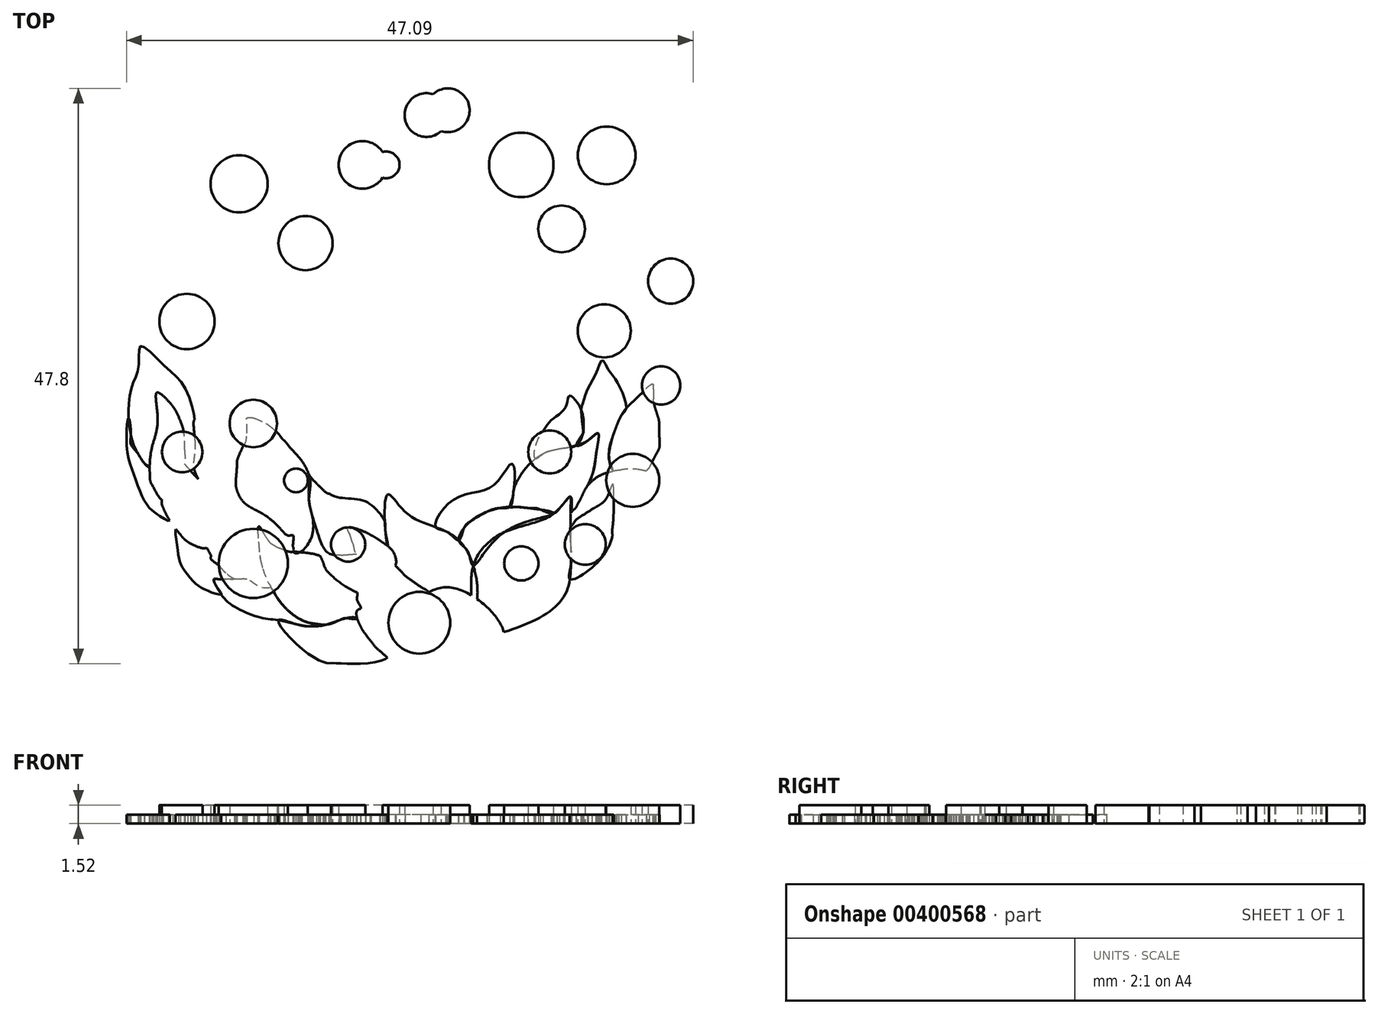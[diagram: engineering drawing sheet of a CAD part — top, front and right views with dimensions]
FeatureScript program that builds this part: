
annotation { "Feature Type Name" : "Feature", "Feature Type Description" : "" }
export const myFeature = defineFeature(function(context is Context, id is Id, definition is map)
    precondition{}
    {
        {
            var Q0;
            Q0=qCreatedBy(makeId("Top.planeOp"),FACE);
            var sketch = newSketch(context, id + "F0", { "sketchPlane" : qUnion([Q0])});
            skCircle(sketch, "E0", {"center": v(13.2, 35.87) * mm, "radius": 2.4 * mm});
            skCircle(sketch, "E1", {"center": v(-7.1, 35.08) * mm, "radius": 1.98 * mm});
            skCircle(sketch, "E2", {"center": v(-5.11, 35.08) * mm, "radius": 1.1 * mm});
            skCircle(sketch, "E3", {"center": v(-21.68, 22.07) * mm, "radius": 2.3 * mm});
            skCircle(sketch, "E4", {"center": v(-16.16, 13.6) * mm, "radius": 1.97 * mm});
            skCircle(sketch, "E5", {"center": v(-16.16, 1.97) * mm, "radius": 2.87 * mm});
            skCircle(sketch, "E6", {"center": v(-2.36, -2.96) * mm, "radius": 2.57 * mm});
            skCircle(sketch, "E7", {"center": v(6.1, 1.97) * mm, "radius": 1.42 * mm});
            skCircle(sketch, "E8", {"center": v(15.37, 8.87) * mm, "radius": 2.2 * mm});
            skCircle(sketch, "E9", {"center": v(13, 21.28) * mm, "radius": 2.2 * mm});
            skCircle(sketch, "E10", {"center": v(9.46, 29.76) * mm, "radius": 1.94 * mm});
            skCircle(sketch, "E11", {"center": v(-11.82, 28.58) * mm, "radius": 2.25 * mm});
            skCircle(sketch, "E12", {"center": v(6.1, 35.08) * mm, "radius": 2.68 * mm});
            skCircle(sketch, "E13", {"center": v(18.52, 25.42) * mm, "radius": 1.87 * mm});
            skSolve(sketch);
        }
        {
            var Q0;
            Q0=qCreatedBy(makeId("Top.planeOp"),FACE);
            var sketch = newSketch(context, id + "F1", { "sketchPlane" : qUnion([Q0])});
            skCircle(sketch, "E14", {"center": v(0, 39.61) * mm, "radius": 1.82 * mm});
            skCircle(sketch, "E15", {"center": v(-1.77, 39.22) * mm, "radius": 1.82 * mm});
            skCircle(sketch, "E16", {"center": v(-17.34, 33.5) * mm, "radius": 2.37 * mm});
            skCircle(sketch, "E17", {"center": v(-22.07, 11.23) * mm, "radius": 1.68 * mm});
            skCircle(sketch, "E18", {"center": v(-12.61, 8.87) * mm, "radius": 0.99 * mm});
            skCircle(sketch, "E19", {"center": v(-8.28, 3.55) * mm, "radius": 1.42 * mm});
            skCircle(sketch, "E20", {"center": v(8.47, 11.23) * mm, "radius": 1.78 * mm});
            skCircle(sketch, "E21", {"center": v(11.43, 3.55) * mm, "radius": 1.7 * mm});
            skCircle(sketch, "E22", {"center": v(17.74, 16.75) * mm, "radius": 1.59 * mm});
            skSolve(sketch);
        }
        {
            var Q0;
            Q0=qCreatedBy(makeId("Top.planeOp"),FACE);
            var sketch = newSketch(context, id + "F2", { "sketchPlane" : qUnion([Q0])});
            skFitSpline(sketch, "E23", {"points": [v(1.92, -3.92) * mm, v(1.92, -1.95) * mm, v(2.12, 1.8) * mm, v(4.68, 4.55) * mm, v(8.82, 6.13) * mm, v(10.2, 7.51) * mm, v(10.2, 4.55) * mm, v(10, 0) * mm, v(7.24, -2.74) * mm, v(1.92, -3.92) * mm]});
            skFitSpline(sketch, "E24", {"points": [v(2.12, 1.8) * mm, v(0, 4.55) * mm, v(-3.4, 6.13) * mm, v(-4.98, 7.7) * mm, v(-5.17, 4.55) * mm, v(-4.38, 1.8) * mm, v(-2.22, 0) * mm, v(1.92, -1.95) * mm, v(2.12, 1.8) * mm]});
            skFitSpline(sketch, "E25", {"points": [v(4.68, -3.92) * mm, v(1.92, -6.28) * mm, v(-4.38, -6.28) * mm, v(-7.54, -1.95) * mm, v(-4.38, -1.95) * mm, v(0, 0) * mm, v(4.68, -3.92) * mm]});
            skFitSpline(sketch, "E26", {"points": [v(0.92, 3.9) * mm, v(1.92, 5.5) * mm, v(4.35, 6.58) * mm, v(6.67, 6.58) * mm, v(8.82, 6.13) * mm, v(4.68, 4.55) * mm, v(2.12, 1.8) * mm, v(1.78, 2.66) * mm, v(1.42, 3.3) * mm, v(0.92, 3.9) * mm]});
            skFitSpline(sketch, "E27", {"points": [v(10.15, 0.66) * mm, v(12.18, 1.8) * mm, v(13.59, 3.9) * mm, v(13.75, 5.54) * mm, v(13.71, 8.57) * mm, v(13.22, 7.45) * mm, v(12.3, 6.66) * mm, v(10.69, 5.62) * mm, v(10.22, 5.06) * mm, v(10.2, 3.62) * mm, v(10.23, 1.8) * mm, v(10.15, 0.66) * mm]});
            skFitSpline(sketch, "E28", {"points": [v(-5.02, -5.85) * mm, v(-7.13, -6.35) * mm, v(-9.49, -6.3) * mm, v(-10.2, -6.27) * mm, v(-12.43, -4.86) * mm, v(-14.09, -2.74) * mm, v(-12.43, -3.12) * mm, v(-10.32, -3.16) * mm, v(-9, -2.74) * mm, v(-7.54, -2.57) * mm, v(-7.23, -3.27) * mm, v(-6.83, -3.92) * mm, v(-6.47, -4.4) * mm, v(-5.59, -5.35) * mm, v(-5.02, -5.85) * mm]});
            skFitSpline(sketch, "E29", {"points": [v(-3.53, 0.94) * mm, v(-4.38, 1.8) * mm, v(-6.3, 2.64) * mm, v(-8.29, 2.68) * mm, v(-9.9, 2.8) * mm, v(-10.65, 3.14) * mm, v(-10.23, 1.8) * mm, v(-9.32, 0.66) * mm, v(-7.54, -0.42) * mm, v(-5.02, -0.92) * mm, v(-3.4, -0.92) * mm, v(-2.11, -0.76) * mm, v(-1.6, -0.44) * mm, v(-2.22, 0) * mm, v(-3.16, 0.66) * mm, v(-3.53, 0.94) * mm]});
            skFitSpline(sketch, "E30", {"points": [v(-10.14, -3.12) * mm, v(-12.43, -2.57) * mm, v(-14.25, -0.76) * mm, v(-15.58, 2.35) * mm, v(-15.7, 5.04) * mm, v(-14.91, 3.9) * mm, v(-12.84, 2.97) * mm, v(-10.56, 2.54) * mm, v(-10.32, 1.96) * mm, v(-9.76, 1.09) * mm, v(-7.54, -0.42) * mm, v(-7.54, -1) * mm, v(-7.23, -1.8) * mm, v(-7.54, -1.95) * mm, v(-7.54, -2.57) * mm, v(-8.42, -2.57) * mm, v(-9, -2.74) * mm, v(-10.14, -3.12) * mm]});
            skFitSpline(sketch, "E31", {"points": [v(-5.02, 3.44) * mm, v(-5.68, 3.9) * mm, v(-6.83, 4.55) * mm, v(-8.29, 4.92) * mm, v(-7.95, 3.9) * mm, v(-7.54, 2.68) * mm, v(-6.3, 2.64) * mm, v(-5.66, 2.47) * mm, v(-5.02, 2.2) * mm, v(-4.38, 1.8) * mm, v(-4.38, 2.64) * mm, v(-5.02, 3.44) * mm]});
            skFitSpline(sketch, "E32", {"points": [v(-14.72, 0) * mm, v(-16.7, 0.66) * mm, v(-19.02, 0.66) * mm, v(-19.43, 0.66) * mm, v(-19.18, 0) * mm, v(-18.44, -1.09) * mm, v(-17.11, -1.95) * mm, v(-15.37, -2.57) * mm, v(-14.09, -2.74) * mm, v(-12.43, -3.12) * mm, v(-11.56, -3.25) * mm, v(-10.32, -3.16) * mm, v(-11.55, -2.95) * mm, v(-12.43, -2.57) * mm, v(-13.26, -1.95) * mm, v(-14.25, -0.76) * mm, v(-14.72, 0) * mm]});
            skFitSpline(sketch, "E33", {"points": [v(-1, 4.98) * mm, v(-0.64, 6.13) * mm, v(0.92, 7.51) * mm, v(3, 8.06) * mm, v(4.35, 9.05) * mm, v(5.33, 10.25) * mm, v(5.57, 9.3) * mm, v(5.4, 7.51) * mm, v(5.17, 6.66) * mm, v(4.35, 6.58) * mm, v(3.3, 6.28) * mm, v(1.92, 5.5) * mm, v(1.34, 4.91) * mm, v(0.92, 3.9) * mm, v(0, 4.55) * mm, v(-1, 4.98) * mm]});
            skFitSpline(sketch, "E34", {"points": [v(5.48, 8.06) * mm, v(6.28, 9.63) * mm, v(7.94, 11.08) * mm, v(9.63, 11.54) * mm, v(11.66, 12.2) * mm, v(12.5, 12.78) * mm, v(12.4, 11.58) * mm, v(12, 9.3) * mm, v(11.13, 7.51) * mm, v(10.23, 6.13) * mm, v(10.2, 7.51) * mm, v(9.7, 7.04) * mm, v(9.3, 6.58) * mm, v(8.82, 6.13) * mm, v(7.7, 6.44) * mm, v(7.24, 6.58) * mm, v(6.67, 6.58) * mm, v(5.57, 6.66) * mm, v(5.17, 6.66) * mm, v(5.4, 7.51) * mm, v(5.48, 8.06) * mm]});
            skFitSpline(sketch, "E35", {"points": [v(11.64, 8.46) * mm, v(12.78, 9.34) * mm, v(14.23, 9.71) * mm, v(15.8, 9.8) * mm, v(17.1, 9.67) * mm, v(18.33, 9.96) * mm, v(18.38, 9.5) * mm, v(18.13, 8.3) * mm, v(17.3, 6.65) * mm, v(16.01, 5.4) * mm, v(14.07, 4.5) * mm, v(13.7, 4.36) * mm, v(13.75, 5.54) * mm, v(13.78, 6.6) * mm, v(13.8, 7.85) * mm, v(13.71, 8.57) * mm, v(13.44, 7.98) * mm, v(13.22, 7.45) * mm, v(12.64, 6.85) * mm, v(12.3, 6.66) * mm, v(11.13, 5.93) * mm, v(10.69, 5.62) * mm, v(10.22, 5.06) * mm, v(10.22, 5.62) * mm, v(10.23, 6.13) * mm, v(10.69, 6.66) * mm, v(11.13, 7.51) * mm, v(11.64, 8.46) * mm]});
            skFitSpline(sketch, "E36", {"points": [v(-5.24, 5.45) * mm, v(-6.1, 6.6) * mm, v(-7.14, 7.23) * mm, v(-8.6, 7.4) * mm, v(-9.88, 7.77) * mm, v(-11.37, 9.13) * mm, v(-11.5, 9.3) * mm, v(-11.5, 9.01) * mm, v(-11.54, 8.55) * mm, v(-11.54, 7.27) * mm, v(-11.29, 6.03) * mm, v(-10.75, 4.29) * mm, v(-9.9, 2.8) * mm, v(-8.88, 2.65) * mm, v(-8.29, 2.68) * mm, v(-7.54, 2.68) * mm, v(-7.88, 3.6) * mm, v(-8.12, 4.3) * mm, v(-8.29, 4.92) * mm, v(-6.83, 4.55) * mm, v(-6.3, 4.28) * mm, v(-5.68, 3.9) * mm, v(-5.02, 3.44) * mm, v(-5.17, 4.55) * mm, v(-5.24, 5.45) * mm]});
            skFitSpline(sketch, "E37", {"points": [v(-17.7, 0.68) * mm, v(-19.02, 1.8) * mm, v(-19.68, 2.66) * mm, v(-20.43, 4.3) * mm, v(-20.6, 6.13) * mm, v(-20.5, 8.06) * mm, v(-20.01, 8.06) * mm, v(-17.53, 6.83) * mm, v(-14.72, 5.62) * mm, v(-12.84, 2.97) * mm, v(-14.4, 3.44) * mm, v(-14.91, 3.9) * mm, v(-15.7, 5.04) * mm, v(-15.7, 3.44) * mm, v(-15.58, 2.35) * mm, v(-14.91, 0.37) * mm, v(-14.72, 0) * mm, v(-15.58, 0) * mm, v(-16.7, 0.66) * mm, v(-17.7, 0.68) * mm]});
            skFitSpline(sketch, "E38", {"points": [v(-16.7, 6.83) * mm, v(-17.53, 8.06) * mm, v(-17.53, 10.48) * mm, v(-16.7, 12.8) * mm, v(-16.7, 14.04) * mm, v(-14.91, 13.46) * mm, v(-13.26, 11.8) * mm, v(-11.5, 9.3) * mm, v(-11.54, 7.27) * mm, v(-11.29, 6.03) * mm, v(-11.29, 4.29) * mm, v(-12.27, 2.9) * mm, v(-12.84, 2.97) * mm, v(-12.84, 4.3) * mm, v(-13.26, 4.29) * mm, v(-14.72, 5.62) * mm, v(-16.7, 6.83) * mm]});
            skFitSpline(sketch, "E39", {"points": [v(7.28, 10.66) * mm, v(7.33, 11.86) * mm, v(7.94, 13) * mm, v(8.66, 13.93) * mm, v(9.8, 14.96) * mm, v(10.1, 15.9) * mm, v(10.69, 15.45) * mm, v(11.22, 14.27) * mm, v(11.22, 12.74) * mm, v(10.69, 11.77) * mm, v(9.63, 11.54) * mm, v(8.58, 11.32) * mm, v(7.94, 11.08) * mm, v(7.28, 10.66) * mm]});
            skFitSpline(sketch, "E40", {"points": [v(16.53, 9.67) * mm, v(17.1, 10.63) * mm, v(17.58, 11.58) * mm, v(17.58, 12.65) * mm, v(17.53, 13.93) * mm, v(17.1, 15.6) * mm, v(17.1, 16.83) * mm, v(16.7, 16.69) * mm, v(16.2, 16.2) * mm, v(15.26, 15.3) * mm, v(14.43, 14.27) * mm, v(13.69, 12.45) * mm, v(13.4, 11.08) * mm, v(13.73, 9.63) * mm, v(14.23, 9.71) * mm, v(15.8, 9.8) * mm, v(16.53, 9.67) * mm]});
            skFitSpline(sketch, "E41", {"points": [v(14.83, 14.85) * mm, v(14.43, 16.34) * mm, v(13.83, 17.42) * mm, v(13.34, 18.07) * mm, v(12.85, 18.85) * mm, v(12.4, 17.97) * mm, v(11.66, 16.54) * mm, v(11.22, 15.3) * mm, v(11.1, 14.7) * mm, v(11.27, 13) * mm, v(11.22, 12.74) * mm, v(10.69, 11.77) * mm, v(11.66, 12.2) * mm, v(12.5, 12.78) * mm, v(12.4, 11.58) * mm, v(12.3, 10.82) * mm, v(12, 9.3) * mm, v(11.64, 8.46) * mm, v(12.78, 9.34) * mm, v(13.73, 9.63) * mm, v(13.44, 10.48) * mm, v(13.4, 11.08) * mm, v(13.69, 12.45) * mm, v(14.08, 13.52) * mm, v(14.43, 14.27) * mm, v(14.83, 14.85) * mm]});
            skFitSpline(sketch, "E42", {"points": [v(-20.03, 3.3) * mm, v(-21.35, 3.6) * mm, v(-22.17, 4.3) * mm, v(-23.1, 5.54) * mm, v(-23.75, 7) * mm, v(-23.63, 8.06) * mm, v(-23.34, 9.63) * mm, v(-23.16, 11.32) * mm, v(-21.35, 9.63) * mm, v(-20.01, 8.06) * mm, v(-20.5, 8.06) * mm, v(-20.63, 7.3) * mm, v(-20.6, 6.13) * mm, v(-20.5, 4.7) * mm, v(-20.43, 4.3) * mm, v(-20.03, 3.3) * mm]});
            skFitSpline(sketch, "E43", {"points": [v(-9.88, 7.77) * mm, v(-10.5, 9.3) * mm, v(-11.39, 10.48) * mm, v(-13.26, 11.8) * mm, v(-12.13, 10.48) * mm, v(-11.5, 9.3) * mm, v(-10.75, 8.46) * mm, v(-9.88, 7.77) * mm]});
            skFitSpline(sketch, "E44", {"points": [v(18.26, 8.84) * mm, v(18.83, 9.5) * mm, v(19.6, 11.08) * mm, v(20, 13.46) * mm, v(19.68, 15.3) * mm, v(19.2, 16.83) * mm, v(18.7, 17.99) * mm, v(18.38, 19.62) * mm, v(18.13, 19.1) * mm, v(17.8, 18.46) * mm, v(17.58, 17.9) * mm, v(17.3, 17.18) * mm, v(17.1, 16.83) * mm, v(17.1, 16.06) * mm, v(17.1, 15.6) * mm, v(17.3, 14.68) * mm, v(17.53, 13.93) * mm, v(17.58, 13.46) * mm, v(17.58, 12.65) * mm, v(17.61, 12.04) * mm, v(17.58, 11.58) * mm, v(17.2, 10.8) * mm, v(17.1, 10.48) * mm, v(16.73, 9.9) * mm, v(16.53, 9.67) * mm, v(17.1, 9.67) * mm, v(17.58, 9.67) * mm, v(18.33, 9.96) * mm, v(18.38, 9.5) * mm, v(18.26, 8.84) * mm]});
            skFitSpline(sketch, "E45", {"points": [v(-18.84, -0.6) * mm, v(-20.01, -0.28) * mm, v(-21.05, 0.39) * mm, v(-22.13, 1.8) * mm, v(-22.44, 3.03) * mm, v(-22.6, 4.83) * mm, v(-22.17, 4.3) * mm, v(-21.61, 3.77) * mm, v(-21.35, 3.6) * mm, v(-20.63, 3.44) * mm, v(-20.03, 3.3) * mm, v(-19.68, 2.66) * mm, v(-19.68, 2.35) * mm, v(-19.02, 1.8) * mm, v(-18.44, 1.17) * mm, v(-17.7, 0.68) * mm, v(-18.44, 0.66) * mm, v(-19.02, 0.66) * mm, v(-19.43, 0.66) * mm, v(-19.18, 0) * mm, v(-18.84, -0.6) * mm]});
            skFitSpline(sketch, "E46", {"points": [v(-13.6, 12.2) * mm, v(-13.72, 13.93) * mm, v(-14.4, 15.6) * mm, v(-15.58, 17.62) * mm, v(-16.7, 18.46) * mm, v(-17.7, 19.3) * mm, v(-19.02, 20.58) * mm, v(-19.02, 19.89) * mm, v(-19.18, 18.8) * mm, v(-19.18, 17.59) * mm, v(-19.18, 15.92) * mm, v(-19.02, 14.77) * mm, v(-18.44, 13.46) * mm, v(-16.95, 11.86) * mm, v(-16.7, 12.8) * mm, v(-16.7, 13.52) * mm, v(-16.7, 14.04) * mm, v(-16.13, 14.04) * mm, v(-14.91, 13.46) * mm, v(-14.32, 13) * mm, v(-13.98, 12.65) * mm, v(-13.6, 12.2) * mm]});
            skFitSpline(sketch, "E47", {"points": [v(-20.43, 8.46) * mm, v(-21.04, 9.96) * mm, v(-21.04, 11.08) * mm, v(-21, 12.2) * mm, v(-21.04, 13.93) * mm, v(-20.01, 13) * mm, v(-19.02, 12.45) * mm, v(-17.7, 11.08) * mm, v(-17.53, 10.48) * mm, v(-17.53, 9.96) * mm, v(-17.62, 8.46) * mm, v(-17.53, 8.06) * mm, v(-16.9, 7) * mm, v(-15.86, 6.28) * mm, v(-16.85, 6.6) * mm, v(-17.53, 6.83) * mm, v(-18.94, 7.51) * mm, v(-19.42, 7.77) * mm, v(-20.01, 8.06) * mm, v(-20.43, 8.46) * mm]});
            skFitSpline(sketch, "E48", {"points": [v(-23.75, 7.3) * mm, v(-24.45, 8.3) * mm, v(-24.76, 9.5) * mm, v(-24.6, 11.58) * mm, v(-24.1, 13.93) * mm, v(-24.17, 16.16) * mm, v(-23.1, 15.3) * mm, v(-22.17, 13.46) * mm, v(-21.9, 10.26) * mm, v(-22.23, 10.63) * mm, v(-23.02, 11.32) * mm, v(-23.16, 11.32) * mm, v(-23.16, 11.08) * mm, v(-23.16, 10.48) * mm, v(-23.34, 9.63) * mm, v(-23.52, 8.46) * mm, v(-23.63, 8.06) * mm, v(-23.75, 7.3) * mm]});
            skFitSpline(sketch, "E49", {"points": [v(-24.78, 9.96) * mm, v(-25.74, 11.08) * mm, v(-26.33, 12.65) * mm, v(-26.54, 14.73) * mm, v(-26.2, 16.83) * mm, v(-25.67, 18.46) * mm, v(-25.53, 20.03) * mm, v(-23.63, 18.46) * mm, v(-21.8, 16.5) * mm, v(-21.04, 13.93) * mm, v(-21.04, 13.52) * mm, v(-21, 12.2) * mm, v(-21, 11.86) * mm, v(-21.04, 11.08) * mm, v(-21.04, 9.67) * mm, v(-20.43, 8.46) * mm, v(-21.35, 9.63) * mm, v(-21.9, 10.26) * mm, v(-21.9, 11.08) * mm, v(-21.9, 12.65) * mm, v(-22.33, 14.04) * mm, v(-22.86, 15.03) * mm, v(-23.22, 15.45) * mm, v(-24.17, 16.16) * mm, v(-24.17, 15.3) * mm, v(-24.1, 14.04) * mm, v(-24.1, 13.46) * mm, v(-24.1, 12.65) * mm, v(-24.6, 11.58) * mm, v(-24.78, 9.96) * mm]});
            skFitSpline(sketch, "E50", {"points": [v(-23.1, 5.54) * mm, v(-24.1, 6.03) * mm, v(-25.11, 7) * mm, v(-26.02, 9.13) * mm, v(-26.68, 11.77) * mm, v(-26.52, 14.04) * mm, v(-26.33, 12.65) * mm, v(-26.33, 11.86) * mm, v(-25.74, 11.08) * mm, v(-25.19, 10.26) * mm, v(-24.78, 9.96) * mm, v(-24.76, 9.13) * mm, v(-24.45, 8.3) * mm, v(-23.75, 7.3) * mm, v(-23.75, 6.83) * mm, v(-23.1, 5.54) * mm]});
            skSolve(sketch);
        }
        {
            var Q0;
            Q0 = qSketchRegion(id + "F0", true);
            var Q1;
            Q1=makeQuery(id+"F1.imprint","IMPRINT",FACE,{"disambiguationData":[TD([[makeQuery(id+"F1.imprint","IMPRINT",EDGE,{"derivedFrom":sQuery(id+"F1.wireOp",EDGE,"E16")}),1.0]])]});
            var Q2;
            {var subQ0=sQuery(id+"F1.wireOp",EDGE,"E15");var subQ1=sQuery(id+"F1.wireOp",EDGE,"E14");var subQ2=makeQuery(id+"F1.imprint","INTERSECT",VERTEX,{"disambiguationData":[OD(0.0)],"derivedFrom":[subQ1,subQ0]});Q2=makeQuery(id+"F1.imprint","IMPRINT",FACE,{"disambiguationData":[TD([[makeQuery(id+"F1.imprint","IMPRINT",EDGE,{"disambiguationData":[TD([[subQ2,1.0]])],"derivedFrom":subQ1}),-1.0]])]});}
            var Q3;
            {var subQ0=sQuery(id+"F1.wireOp",EDGE,"E15");var subQ1=sQuery(id+"F1.wireOp",EDGE,"E14");var subQ2=makeQuery(id+"F1.imprint","INTERSECT",VERTEX,{"disambiguationData":[OD(0.0)],"derivedFrom":[subQ1,subQ0]});Q3=makeQuery(id+"F1.imprint","IMPRINT",FACE,{"disambiguationData":[TD([[makeQuery(id+"F1.imprint","IMPRINT",EDGE,{"disambiguationData":[TD([[subQ2,1.0]])],"derivedFrom":subQ1}),1.0]])]});}
            var Q4;
            {var subQ0=sQuery(id+"F1.wireOp",EDGE,"E15");var subQ1=sQuery(id+"F1.wireOp",EDGE,"E14");var subQ2=makeQuery(id+"F1.imprint","INTERSECT",VERTEX,{"disambiguationData":[OD(0.0)],"derivedFrom":[subQ1,subQ0]});Q4=makeQuery(id+"F1.imprint","IMPRINT",FACE,{"disambiguationData":[TD([[makeQuery(id+"F1.imprint","IMPRINT",EDGE,{"disambiguationData":[TD([[subQ2,-1.0]])],"derivedFrom":subQ1}),1.0]])]});}
            var Q5;
            Q5=makeQuery(id+"F1.imprint","IMPRINT",FACE,{"disambiguationData":[TD([[makeQuery(id+"F1.imprint","IMPRINT",EDGE,{"derivedFrom":sQuery(id+"F1.wireOp",EDGE,"E17")}),1.0]])]});
            var Q6;
            Q6=makeQuery(id+"F1.imprint","IMPRINT",FACE,{"disambiguationData":[TD([[makeQuery(id+"F1.imprint","IMPRINT",EDGE,{"derivedFrom":sQuery(id+"F1.wireOp",EDGE,"E18")}),1.0]])]});
            var Q7;
            Q7=makeQuery(id+"F1.imprint","IMPRINT",FACE,{"disambiguationData":[TD([[makeQuery(id+"F1.imprint","IMPRINT",EDGE,{"derivedFrom":sQuery(id+"F1.wireOp",EDGE,"E19")}),1.0]])]});
            var Q8;
            Q8=makeQuery(id+"F1.imprint","IMPRINT",FACE,{"disambiguationData":[TD([[makeQuery(id+"F1.imprint","IMPRINT",EDGE,{"derivedFrom":sQuery(id+"F1.wireOp",EDGE,"E21")}),1.0]])]});
            var Q9;
            Q9=makeQuery(id+"F1.imprint","IMPRINT",FACE,{"disambiguationData":[TD([[makeQuery(id+"F1.imprint","IMPRINT",EDGE,{"derivedFrom":sQuery(id+"F1.wireOp",EDGE,"E20")}),1.0]])]});
            var Q10;
            Q10=makeQuery(id+"F1.imprint","IMPRINT",FACE,{"disambiguationData":[TD([[makeQuery(id+"F1.imprint","IMPRINT",EDGE,{"derivedFrom":sQuery(id+"F1.wireOp",EDGE,"E22")}),1.0]])]});
            extrude(context, id + "F3", {"entities" : qUnion([Q0, Q1, Q2, Q3, Q4, Q5, Q6, Q7, Q8, Q9, Q10]), "depth" : 1.52 * mm});
        }
        {
            var Q0;
            {var subQ1=sQuery(id+"F2.wireOp",EDGE,"E30");var subQ7=sQuery(id+"F2.wireOp",EDGE,"E25");var subQ28=makeQuery(id+"F2.imprint","INTERSECT",VERTEX,{"disambiguationData":[OD(1.0)],"derivedFrom":[subQ7,subQ1]});Q0=makeQuery(id+"F2.imprint","IMPRINT",FACE,{"disambiguationData":[TD([[makeQuery(id+"F2.imprint","IMPRINT",EDGE,{"disambiguationData":[TD([[subQ28,-1.0]])],"derivedFrom":subQ7}),1.0]])]});}
            var Q1;
            {var subQ0=sQuery(id+"F2.wireOp",EDGE,"E26");var subQ1=sQuery(id+"F2.wireOp",EDGE,"E24");var subQ2=makeQuery(id+"F2.imprint","INTERSECT",VERTEX,{"disambiguationData":[OD(0.0)],"derivedFrom":[subQ1,subQ0]});Q1=makeQuery(id+"F2.imprint","IMPRINT",FACE,{"disambiguationData":[TD([[makeQuery(id+"F2.imprint","IMPRINT",EDGE,{"disambiguationData":[TD([[subQ2,-1.0]])],"derivedFrom":subQ1}),1.0]])]});}
            var Q2;
            {var subQ1=sQuery(id+"F2.wireOp",EDGE,"E38");var subQ13=sQuery(id+"F2.wireOp",EDGE,"E36");var subQ23=makeQuery(id+"F2.imprint","INTERSECT",VERTEX,{"disambiguationData":[OD(1.0)],"derivedFrom":[subQ13,subQ1]});Q2=makeQuery(id+"F2.imprint","IMPRINT",FACE,{"disambiguationData":[TD([[makeQuery(id+"F2.imprint","IMPRINT",EDGE,{"disambiguationData":[TD([[subQ23,-1.0]])],"derivedFrom":subQ13}),-1.0]])]});}
            var Q3;
            {var subQ0=sQuery(id+"F2.wireOp",EDGE,"E49");var subQ10=sQuery(id+"F2.wireOp",EDGE,"E42");var subQ12=makeQuery(id+"F2.imprint","INTERSECT",VERTEX,{"disambiguationData":[OD(1.0)],"derivedFrom":[subQ10,subQ0]});Q3=makeQuery(id+"F2.imprint","IMPRINT",FACE,{"disambiguationData":[TD([[makeQuery(id+"F2.imprint","IMPRINT",EDGE,{"disambiguationData":[TD([[subQ12,-1.0]])],"derivedFrom":subQ10}),1.0]])]});}
            var Q4;
            {var subQ0=sQuery(id+"F2.wireOp",EDGE,"E45");var subQ6=sQuery(id+"F2.wireOp",EDGE,"E32");var subQ18=makeQuery(id+"F2.imprint","INTERSECT",VERTEX,{"disambiguationData":[OD(2.0)],"derivedFrom":[subQ6,subQ0]});Q4=makeQuery(id+"F2.imprint","IMPRINT",FACE,{"disambiguationData":[TD([[makeQuery(id+"F2.imprint","IMPRINT",EDGE,{"disambiguationData":[TD([[subQ18,-1.0]])],"derivedFrom":subQ6}),-1.0]])]});}
            var Q5;
            {var subQ1=sQuery(id+"F2.wireOp",EDGE,"E28");var subQ9=sQuery(id+"F2.wireOp",EDGE,"E25");var subQ14=makeQuery(id+"F2.imprint","INTERSECT",VERTEX,{"disambiguationData":[OD(0.0)],"derivedFrom":[subQ9,subQ1]});Q5=makeQuery(id+"F2.imprint","IMPRINT",FACE,{"disambiguationData":[TD([[makeQuery(id+"F2.imprint","IMPRINT",EDGE,{"disambiguationData":[TD([[subQ14,-1.0]])],"derivedFrom":subQ9}),1.0]])]});}
            var Q6;
            {var subQ1=sQuery(id+"F2.wireOp",EDGE,"E23");var subQ8=sQuery(id+"F2.wireOp",EDGE,"E26");var subQ9=makeQuery(id+"F2.imprint","INTERSECT",VERTEX,{"disambiguationData":[OD(0.0)],"derivedFrom":[subQ1,subQ8]});Q6=makeQuery(id+"F2.imprint","IMPRINT",FACE,{"disambiguationData":[TD([[makeQuery(id+"F2.imprint","IMPRINT",EDGE,{"disambiguationData":[TD([[subQ9,-1.0]])],"derivedFrom":subQ1}),-1.0]])]});}
            var Q7;
            {var subQ1=sQuery(id+"F2.wireOp",EDGE,"E23");var subQ3=sQuery(id+"F2.wireOp",EDGE,"E34");var subQ15=makeQuery(id+"F2.imprint","INTERSECT",VERTEX,{"disambiguationData":[OD(1.0)],"derivedFrom":[subQ1,subQ3]});Q7=makeQuery(id+"F2.imprint","IMPRINT",FACE,{"disambiguationData":[TD([[makeQuery(id+"F2.imprint","IMPRINT",EDGE,{"disambiguationData":[TD([[subQ15,-1.0]])],"derivedFrom":subQ1}),1.0]])]});}
            var Q8;
            {var subQ0=sQuery(id+"F2.wireOp",EDGE,"E44");var subQ1=sQuery(id+"F2.wireOp",EDGE,"E40");var subQ26=makeQuery(id+"F2.imprint","INTERSECT",VERTEX,{"disambiguationData":[OD(3.0)],"derivedFrom":[subQ1,subQ0]});Q8=makeQuery(id+"F2.imprint","IMPRINT",FACE,{"disambiguationData":[TD([[makeQuery(id+"F2.imprint","IMPRINT",EDGE,{"disambiguationData":[TD([[subQ26,-1.0]])],"derivedFrom":subQ1}),1.0]])]});}
            var Q9;
            {var subQ1=sQuery(id+"F2.wireOp",EDGE,"E33");var subQ4=sQuery(id+"F2.wireOp",EDGE,"E24");var subQ5=makeQuery(id+"F2.imprint","INTERSECT",VERTEX,{"disambiguationData":[OD(0.0)],"derivedFrom":[subQ4,subQ1]});Q9=makeQuery(id+"F2.imprint","IMPRINT",FACE,{"disambiguationData":[TD([[makeQuery(id+"F2.imprint","IMPRINT",EDGE,{"disambiguationData":[TD([[subQ5,1.0]])],"derivedFrom":subQ4}),-1.0]])]});}
            var Q10;
            {var subQ1=sQuery(id+"F2.wireOp",EDGE,"E27");var subQ10=sQuery(id+"F2.wireOp",EDGE,"E23");var subQ14=makeQuery(id+"F2.imprint","INTERSECT",VERTEX,{"disambiguationData":[OD(0.0)],"derivedFrom":[subQ10,subQ1]});Q10=makeQuery(id+"F2.imprint","IMPRINT",FACE,{"disambiguationData":[TD([[makeQuery(id+"F2.imprint","IMPRINT",EDGE,{"disambiguationData":[TD([[subQ14,1.0]])],"derivedFrom":subQ10}),1.0]])]});}
            var Q11;
            {var subQ0=sQuery(id+"F2.wireOp",EDGE,"E41");var subQ14=sQuery(id+"F2.wireOp",EDGE,"E34");var subQ15=makeQuery(id+"F2.imprint","INTERSECT",VERTEX,{"disambiguationData":[OD(1.0)],"derivedFrom":[subQ14,subQ0]});Q11=makeQuery(id+"F2.imprint","IMPRINT",FACE,{"disambiguationData":[TD([[makeQuery(id+"F2.imprint","IMPRINT",EDGE,{"disambiguationData":[TD([[subQ15,-1.0]])],"derivedFrom":subQ14}),1.0]])]});}
            var Q12;
            {var subQ1=sQuery(id+"F2.wireOp",EDGE,"E36");var subQ5=sQuery(id+"F2.wireOp",EDGE,"E24");var subQ19=makeQuery(id+"F2.imprint","INTERSECT",VERTEX,{"disambiguationData":[OD(0.0)],"derivedFrom":[subQ5,subQ1]});Q12=makeQuery(id+"F2.imprint","IMPRINT",FACE,{"disambiguationData":[TD([[makeQuery(id+"F2.imprint","IMPRINT",EDGE,{"disambiguationData":[TD([[subQ19,-1.0]])],"derivedFrom":subQ5}),-1.0]])]});}
            var Q13;
            {var subQ1=sQuery(id+"F2.wireOp",EDGE,"E26");var subQ9=sQuery(id+"F2.wireOp",EDGE,"E33");var subQ12=makeQuery(id+"F2.imprint","INTERSECT",VERTEX,{"disambiguationData":[OD(0.0)],"derivedFrom":[subQ1,subQ9]});Q13=makeQuery(id+"F2.imprint","IMPRINT",FACE,{"disambiguationData":[TD([[makeQuery(id+"F2.imprint","IMPRINT",EDGE,{"disambiguationData":[TD([[subQ12,-1.0]])],"derivedFrom":subQ1}),-1.0]])]});}
            var Q14;
            {var subQ0=sQuery(id+"F2.wireOp",EDGE,"E39");var subQ1=sQuery(id+"F2.wireOp",EDGE,"E34");var subQ2=makeQuery(id+"F2.imprint","INTERSECT",VERTEX,{"disambiguationData":[OD(0.0)],"derivedFrom":[subQ1,subQ0]});Q14=makeQuery(id+"F2.imprint","IMPRINT",FACE,{"disambiguationData":[TD([[makeQuery(id+"F2.imprint","IMPRINT",EDGE,{"disambiguationData":[TD([[subQ2,-1.0]])],"derivedFrom":subQ1}),1.0]])]});}
            var Q15;
            {var subQ0=sQuery(id+"F2.wireOp",EDGE,"E50");var subQ4=sQuery(id+"F2.wireOp",EDGE,"E42");var subQ5=makeQuery(id+"F2.imprint","INTERSECT",VERTEX,{"disambiguationData":[OD(0.0)],"derivedFrom":[subQ4,subQ0]});Q15=makeQuery(id+"F2.imprint","IMPRINT",FACE,{"disambiguationData":[TD([[makeQuery(id+"F2.imprint","IMPRINT",EDGE,{"disambiguationData":[TD([[subQ5,-1.0]])],"derivedFrom":subQ4}),1.0]])]});}
            var Q16;
            {var subQ1=sQuery(id+"F2.wireOp",EDGE,"E32");var subQ7=sQuery(id+"F2.wireOp",EDGE,"E28");var subQ21=makeQuery(id+"F2.imprint","INTERSECT",VERTEX,{"disambiguationData":[OD(0.0)],"derivedFrom":[subQ7,subQ1]});Q16=makeQuery(id+"F2.imprint","IMPRINT",FACE,{"disambiguationData":[TD([[makeQuery(id+"F2.imprint","IMPRINT",EDGE,{"disambiguationData":[TD([[subQ21,-1.0]])],"derivedFrom":subQ7}),1.0]])]});}
            extrude(context, id + "F4", {"entities" : qUnion([Q0, Q1, Q2, Q3, Q4, Q5, Q6, Q7, Q8, Q9, Q10, Q11, Q12, Q13, Q14, Q15, Q16]), "depth" : 0.74 * mm});
        }
    });
